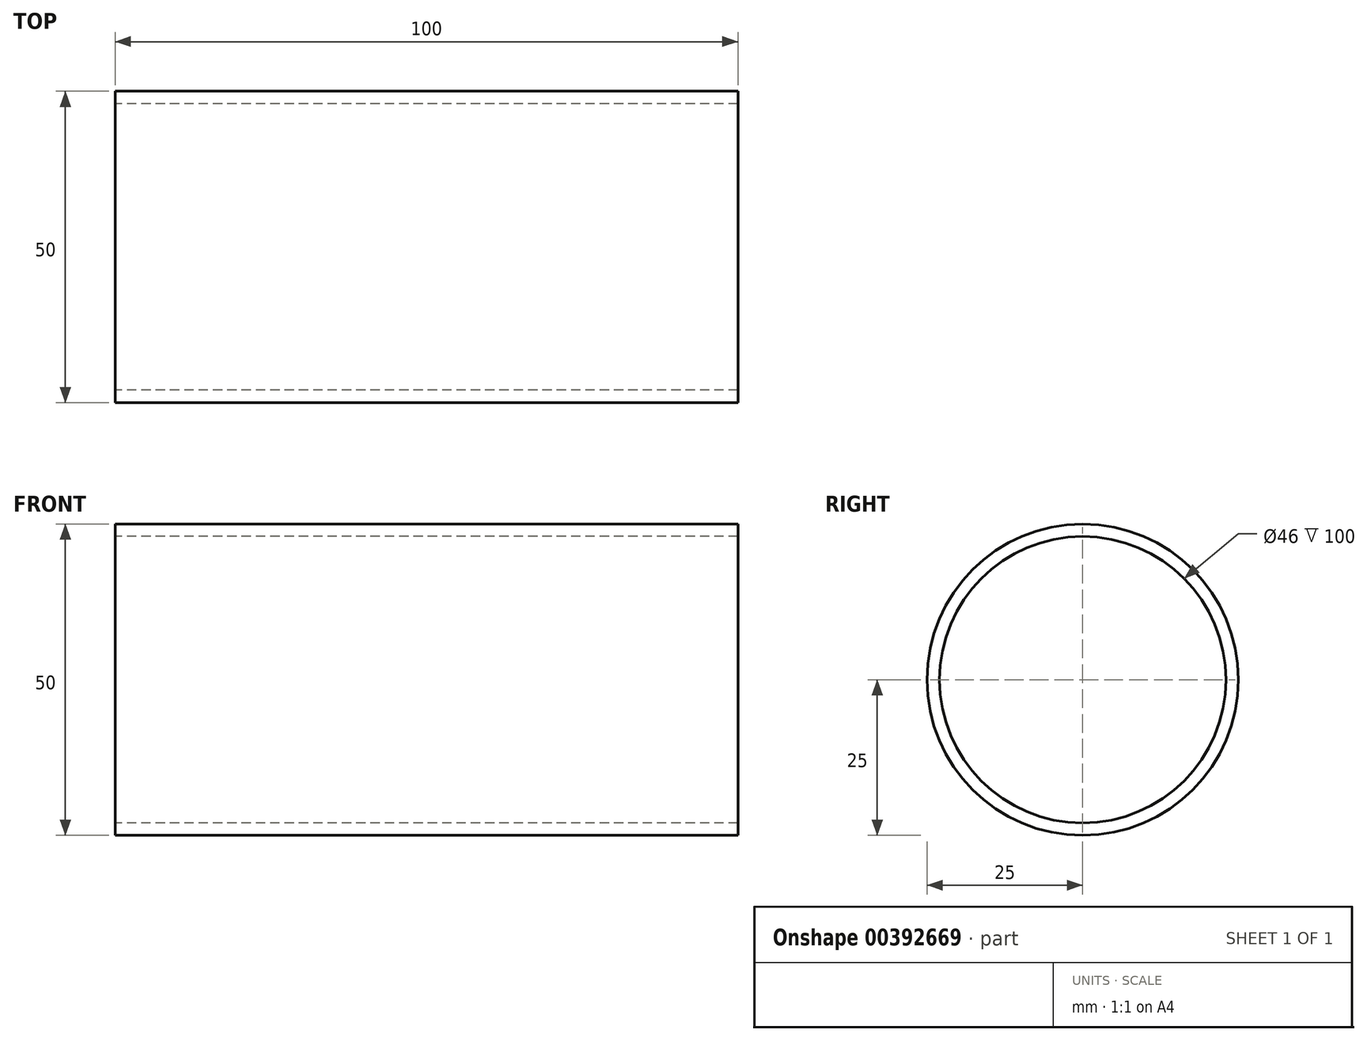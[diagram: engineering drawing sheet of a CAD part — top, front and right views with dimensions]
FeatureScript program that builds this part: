
annotation { "Feature Type Name" : "Feature", "Feature Type Description" : "" }
export const myFeature = defineFeature(function(context is Context, id is Id, definition is map)
    precondition{}
    {
        {
            var Q0;
            Q0=qCreatedBy(makeId("Right.planeOp"),FACE);
            var sketch = newSketch(context, id + "F0", { "sketchPlane" : qUnion([Q0])});
            skCircle(sketch, "E0", {"center": v(0, 0) * mm, "radius": 23 * mm});
            skCircle(sketch, "E1", {"center": v(0, 0) * mm, "radius": 25 * mm});
            skSolve(sketch);
        }
        {
            var Q0;
            Q0 = qSketchRegion(id + "F0", true);
            extrude(context, id + "F1", {"entities" : qUnion([Q0]), "endBound" : BoundingType.SYMMETRIC, "depth" : 100 * mm});
        }
    });
